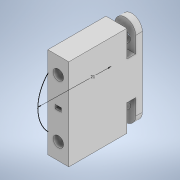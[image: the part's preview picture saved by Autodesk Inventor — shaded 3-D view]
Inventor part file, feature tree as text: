
AUTODESK INVENTOR PART (.ipt)
format: ipt  version: 2020 (Build 240168000, 168)  size: 181,760 bytes
history: native  units: mm
features: sketch x5, extrude x3, fillet x1
ambient origin geometry x8: Origin, YZ Plane, XZ Plane, XY Plane, X Axis, Y Axis, Z Axis, Center Point
bodies: Solid1 (feature_tree)
feature tree (9):
  extrude  "Extrusion1"  Depth=3.0mm
  extrude  "Extrusion2"  Depth=26.0mm
  extrude  "Extrusion3"  Depth=6.0mm
  fillet  "Fillet1"  Radius=1.55mm
  sketch  "Sketch5"  dims[d8=1.1mm d9=21.0mm d10=0.0mm d11=21.0mm d12=2.0mm d14=4.4mm d15=2.5mm d16=0.0mm d17=0.0mm d18=5.5mm d19=0.1mm d20=26.0mm d21=0.0mm d22=3.0mm d23=21.0mm]
  sketch  "Sketch2"  dims[d2=16.5mm d3=26.0mm]
  sketch  "Sketch1"  dims[d0=3.0mm d1=3.0mm]
  sketch  "Sketch3"  dims[d4=6.0mm d5=0.85mm d6=1.55mm]
  sketch  "Sketch4"  dims[d7=1.8mm]
